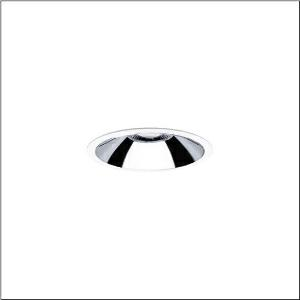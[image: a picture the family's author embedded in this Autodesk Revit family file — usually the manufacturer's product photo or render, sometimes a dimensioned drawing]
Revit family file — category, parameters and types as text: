
# Revit family: lunis_21_l_51db15dd42
name_source: partatom
category: Lighting Fixtures
units: mm (PartAtom-declared; Revit-internal decimal feet)

## family parameters
Cut with Voids When Loaded = No
Host = Face
Light Source = No
Part Type = Normal
Room Calculation Point = No
Round Connector Dimension = Use Diameter
Shared = No

## types (1)
- Lunis 21 L (1 x LED, 1700 lm, 13.8 W, 4000K)
    Apparent Load = 14 VA
    CIE Flux Codes = 90 99 100 100 100
    Color Rendering = 80
    Color Temperature = 4000K
    Default Elevation = 1800 mm
    Description = Lunis 21,  L, downlight, of PC, light emission: direct distribution, LED rated luminous flux: 1.700lm, light colour: 840, control gear: ECG DALI, with terminal, 5-pole, mains connection: 220..240V, AC, housing, round, of diecast aluminium, traffic white (RAL 9016), diameter: 162mm, protection rating (complete): IP20, protection rating (on room side): IP54, insulation class (complete): insulation class II (safety insulation), certification: CE, impact resistance: IK02, packaging unit: 1 piece
    Height = 0 mm  [stored 0 ft]
    Lamp = 1 x LED
    Lamp Light Flux = 1700 lm
    Lamp Power = 13.8 W
    Lamp count = 1
    Length = 162 mm
    Luminous efficacy = 123 lm/W
    Manufacturer = Siteco
    ModVariant = No
    Model = 51DB15DD42
    Mounting Place = Ceiling
    Mounting Type = Recessed
    Number of Poles = 1
    OnlyDefault = Yes
    Power Factor = 1
    Product Name = Lunis 21 L
    Product group = downlight
    ProductGroupID = 400
    Protection Class = Protection class II
    Protection Degree = IP 20
    RLX_Detail_Level = 1
    RLX_Emergency_Light_Flux = 0 lm
    RLX_Emergency_Type = 0
    RLX_Emergency_Type_DB = No
    RlxData = <blob elided: 21229 chars, md5=6db3120a>
    Socket = socket
    Standby Power = 0 W
    System Light Flux = 1700 lm
    System Power = 14 W
    Type Comments = Product without accessories
    Type Image = l_1287387.jpg
    URL = http://relux.com
    VarID = ---
    Voltage = 0 V
    Weight = 0.00 kg
    Width = 0 mm  [stored 0 ft]

note: [stored X ft] marks values corroborated as IEEE doubles in the binary element streams (Revit-internal decimal feet)

## geometry (parser evidence)
native form markers: Blend x4, Sweep x10
no freeform markers — native parametric forms only
